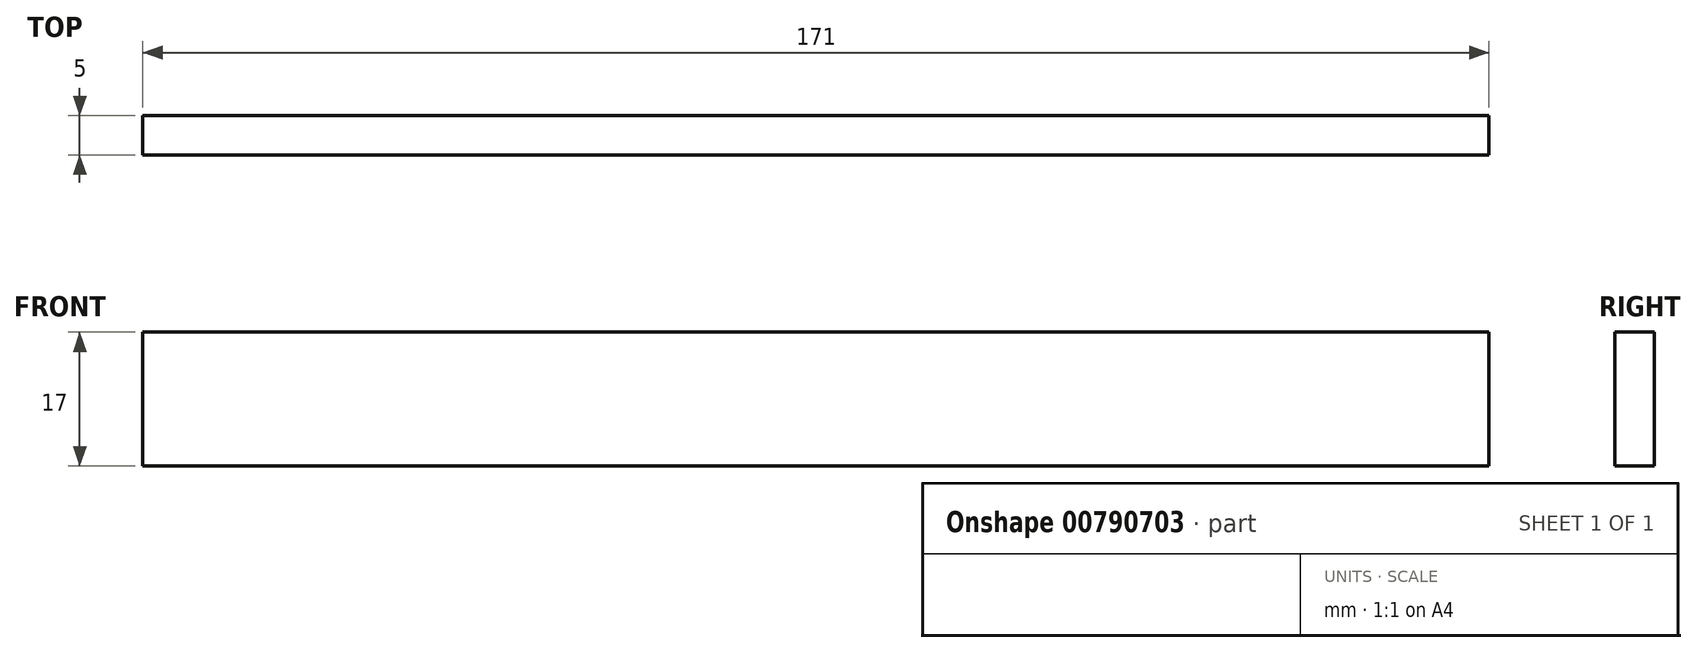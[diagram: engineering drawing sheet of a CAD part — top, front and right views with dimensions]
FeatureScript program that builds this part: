
annotation { "Feature Type Name" : "Feature", "Feature Type Description" : "" }
export const myFeature = defineFeature(function(context is Context, id is Id, definition is map)
    precondition{}
    {
        {
            var Q0;
            Q0=qCreatedBy(makeId("Top.planeOp"),FACE);
            var sketch = newSketch(context, id + "F0", { "sketchPlane" : qUnion([Q0])});
            skLineSegment(sketch, "E0.bottom", {"start": v(85.5, 2.5) * mm, "end": v(-85.5, 2.5) * mm});
            skLineSegment(sketch, "E0.top", {"start": v(85.5, -2.5) * mm, "end": v(-85.5, -2.5) * mm});
            skLineSegment(sketch, "E0.left", {"start": v(85.5, 2.5) * mm, "end": v(85.5, -2.5) * mm});
            skLineSegment(sketch, "E0.right", {"start": v(-85.5, 2.5) * mm, "end": v(-85.5, -2.5) * mm});
            skPoint(sketch, "E0.middle", {"position": v(0, 0) * mm});
            skSolve(sketch);
        }
        {
            var Q0;
            Q0=makeQuery(id+"F0.imprint","IMPRINT",FACE,{"disambiguationData":[TD([[makeQuery(id+"F0.imprint","IMPRINT",EDGE,{"derivedFrom":sQuery(id+"F0.wireOp",EDGE,"E0.bottom")}),1.0]])]});
            extrude(context, id + "F1", {"entities" : qUnion([Q0]), "depth" : 17 * mm, "offsetDistance" : 25 * mm});
        }
    });
